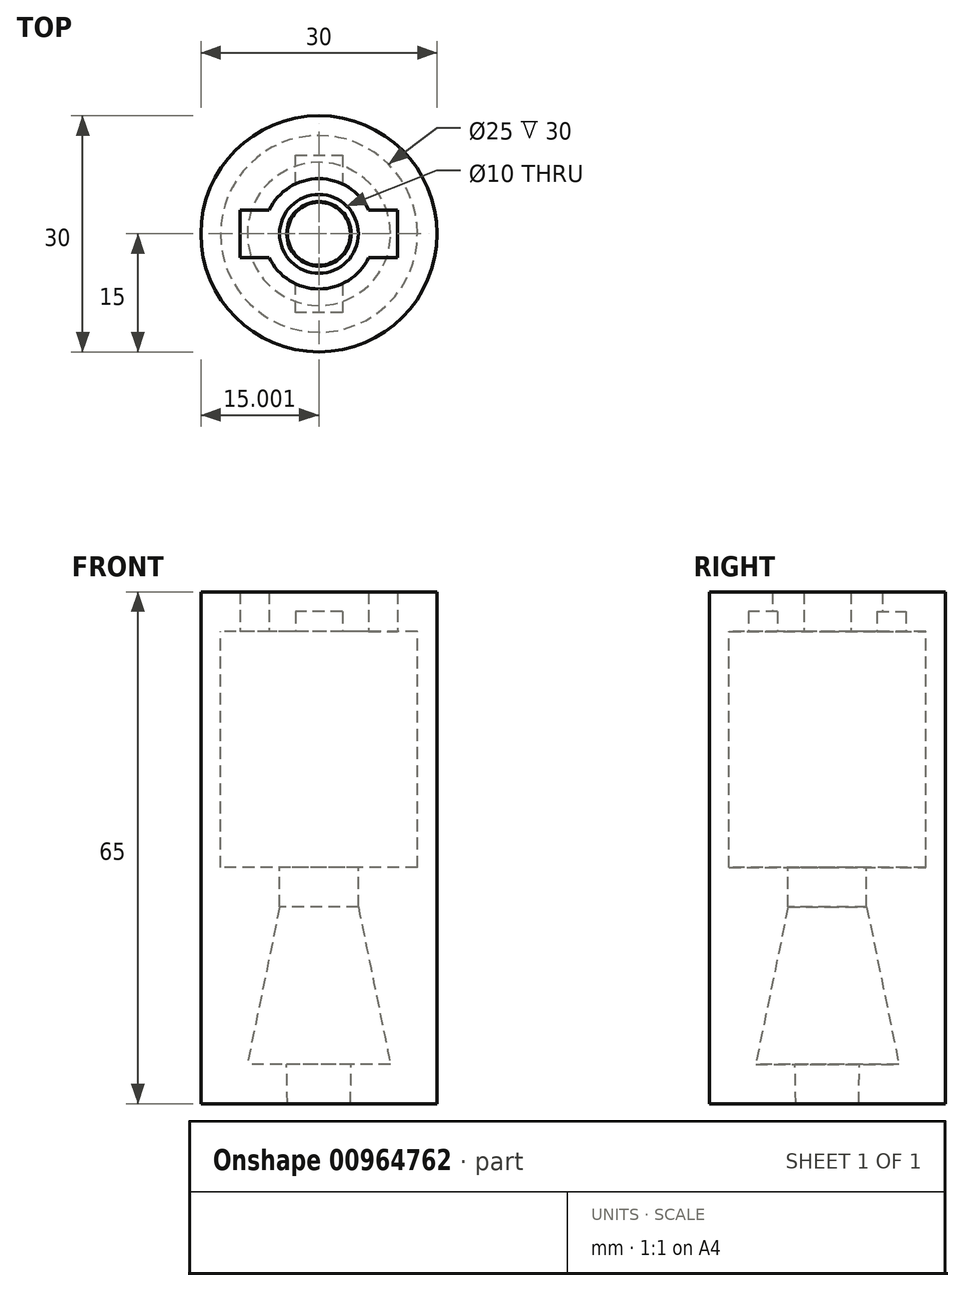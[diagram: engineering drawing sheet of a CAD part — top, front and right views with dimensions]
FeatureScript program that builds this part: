
annotation { "Feature Type Name" : "Feature", "Feature Type Description" : "" }
export const myFeature = defineFeature(function(context is Context, id is Id, definition is map)
    precondition{}
    {
        {
            var Q0;
            Q0=qCreatedBy(makeId("Front.planeOp"),FACE);
            var sketch = newSketch(context, id + "F0", { "sketchPlane" : qUnion([Q0])});
            skArc(sketch, "E0", {"start": v(-36.6, 33.12) * mm, "mid": v(-51.6, 48.12) * mm, "end": v(-66.6, 33.12) * mm});
            skArc(sketch, "E1", {"start": v(-45.27, 36.12) * mm, "mid": v(-46.65, 38.07) * mm, "end": v(-48.6, 39.45) * mm});
            skLineSegment(sketch, "E2.bottom", {"start": v(-54.6, 43.12) * mm, "end": v(-48.6, 43.12) * mm});
            skPoint(sketch, "E3", {"position": v(-51.6, 43.12) * mm});
            skArc(sketch, "E4.trimOffspring", {"start": v(-54.6, 39.45) * mm, "mid": v(-56.55, 38.07) * mm, "end": v(-57.92, 36.12) * mm});
            skCircle(sketch, "E5", {"center": v(-51.6, 33.12) * mm, "radius": 15 * mm});
            skArc(sketch, "E6", {"start": v(-48.6, 26.8) * mm, "mid": v(-46.65, 28.17) * mm, "end": v(-45.27, 30.12) * mm});
            skLineSegment(sketch, "E7", {"start": v(-48.6, 43.12) * mm, "end": v(-48.6, 39.45) * mm});
            skLineSegment(sketch, "E8", {"start": v(-48.6, 23.12) * mm, "end": v(-54.6, 23.12) * mm});
            skLineSegment(sketch, "E9", {"start": v(-54.6, 23.12) * mm, "end": v(-54.6, 26.8) * mm});
            skLineSegment(sketch, "E10.trimOffspring", {"start": v(-54.6, 39.45) * mm, "end": v(-54.6, 43.12) * mm});
            skLineSegment(sketch, "E11.trimOffspring", {"start": v(-48.6, 26.8) * mm, "end": v(-48.6, 23.12) * mm});
            skArc(sketch, "E12.1.0", {"start": v(-57.92, 30.12) * mm, "mid": v(-56.55, 28.17) * mm, "end": v(-54.6, 26.8) * mm});
            skLineSegment(sketch, "E12.1.1", {"start": v(-61.6, 36.12) * mm, "end": v(-57.92, 36.12) * mm});
            skLineSegment(sketch, "E12.1.2", {"start": v(-41.6, 36.12) * mm, "end": v(-41.6, 30.12) * mm});
            skLineSegment(sketch, "E12.1.4", {"start": v(-61.6, 30.12) * mm, "end": v(-61.6, 36.12) * mm});
            skLineSegment(sketch, "E12.1.5", {"start": v(-41.6, 30.12) * mm, "end": v(-45.27, 30.12) * mm});
            skPoint(sketch, "E12.1.6", {"position": v(-41.6, 33.12) * mm});
            skLineSegment(sketch, "E12.1.7", {"start": v(-45.27, 36.12) * mm, "end": v(-41.6, 36.12) * mm});
            skLineSegment(sketch, "E12.1.9", {"start": v(-57.92, 30.12) * mm, "end": v(-61.6, 30.12) * mm});
            skPoint(sketch, "E12.2.6", {"position": v(-51.6, 23.12) * mm});
            skArc(sketch, "E12.2.8", {"start": v(-57.92, 30.12) * mm, "mid": v(-56.55, 28.17) * mm, "end": v(-54.6, 26.8) * mm});
            skLineSegment(sketch, "E12.anchor1", {"start": v(-51.6, 33.12) * mm, "end": v(-54.6, 23.12) * mm, "construction": true});
            skLineSegment(sketch, "E12.anchor2", {"start": v(-51.6, 33.12) * mm, "end": v(-48.6, 43.12) * mm, "construction": true});
            skPoint(sketch, "E13.orphan", {"position": v(-51.6, 40.12) * mm});
            skPoint(sketch, "E14.orphan", {"position": v(-44.6, 33.12) * mm});
            skPoint(sketch, "E15.orphan", {"position": v(-51.6, 26.12) * mm});
            skPoint(sketch, "E16.orphan", {"position": v(-58.6, 33.12) * mm});
            skSolve(sketch);
        }
        {
            var Q0;
            Q0=makeQuery(id+"F0.imprint","IMPRINT",FACE,{"disambiguationData":[TD([[makeQuery(id+"F0.imprint","IMPRINT",EDGE,{"derivedFrom":sQuery(id+"F0.wireOp",EDGE,"E5")}),1.0]])]});
            extrude(context, id + "F1", {"entities" : qUnion([Q0]), "depth" : 2.5 * mm, "offsetDistance" : 25 * mm});
        }
        {
            var Q0;
            Q0=makeQuery(id+"F1.opExtrude","CAP_FACE",FACE,{"disambiguationData":[OSD([sQuery(id+"F0.wireOp",EDGE,"E2.bottom"),sQuery(id+"F0.wireOp",EDGE,"E5"),sQuery(id+"F0.wireOp",EDGE,"E6"),sQuery(id+"F0.wireOp",EDGE,"E7"),sQuery(id+"F0.wireOp",EDGE,"E8"),sQuery(id+"F0.wireOp",EDGE,"E9"),sQuery(id+"F0.wireOp",EDGE,"E10.trimOffspring"),sQuery(id+"F0.wireOp",EDGE,"E11.trimOffspring"),sQuery(id+"F0.wireOp",EDGE,"E4.trimOffspring")])],"isStart":true});
            var sketch = newSketch(context, id + "F2", { "sketchPlane" : qUnion([Q0])});
            skArc(sketch, "E17", {"start": v(64.43, 40.9) * mm, "mid": v(36.77, 30.85) * mm, "end": v(66.16, 29.54) * mm});
            skArc(sketch, "E18", {"start": v(57.92, 36.12) * mm, "mid": v(51.6, 40.12) * mm, "end": v(45.27, 36.12) * mm});
            skLineSegment(sketch, "E19.bottom", {"start": v(41.6, 30.12) * mm, "end": v(41.6, 36.12) * mm});
            skPoint(sketch, "E20", {"position": v(41.6, 33.12) * mm});
            skArc(sketch, "E21.trimOffspring", {"start": v(45.27, 30.12) * mm, "mid": v(51.6, 26.12) * mm, "end": v(57.92, 30.12) * mm});
            skCircle(sketch, "E22", {"center": v(51.6, 33.12) * mm, "radius": 15 * mm});
            skLineSegment(sketch, "E23", {"start": v(41.6, 36.12) * mm, "end": v(45.27, 36.12) * mm});
            skLineSegment(sketch, "E24", {"start": v(61.6, 36.12) * mm, "end": v(61.6, 30.12) * mm});
            skLineSegment(sketch, "E25", {"start": v(61.6, 30.12) * mm, "end": v(57.92, 30.12) * mm});
            skLineSegment(sketch, "E26.trimOffspring", {"start": v(45.27, 30.12) * mm, "end": v(41.6, 30.12) * mm});
            skLineSegment(sketch, "E27.trimOffspring", {"start": v(57.92, 36.12) * mm, "end": v(61.6, 36.12) * mm});
            skArc(sketch, "E28.0", {"start": v(54.6, 39.45) * mm, "mid": v(56.55, 38.07) * mm, "end": v(57.92, 36.12) * mm});
            skArc(sketch, "E28.2", {"start": v(48.6, 26.8) * mm, "mid": v(46.65, 28.17) * mm, "end": v(45.27, 30.12) * mm});
            skArc(sketch, "E29.trimOffspring", {"start": v(45.27, 36.12) * mm, "mid": v(46.65, 38.07) * mm, "end": v(48.6, 39.45) * mm});
            skArc(sketch, "E30.trimOffspring", {"start": v(57.92, 30.12) * mm, "mid": v(56.55, 28.17) * mm, "end": v(54.6, 26.8) * mm});
            skSolve(sketch);
        }
        {
            var Q0;
            Q0 = qSketchRegion(id + "F2", true);
            extrude(context, id + "F3", {"entities" : qUnion([Q0]), "operationType" : NewBodyOperationType.ADD, "depth" : 2.5 * mm, "offsetDistance" : 25 * mm});
        }
        {
            var Q0;
            Q0=qCreatedBy(makeId("Front.planeOp"),FACE);
            var sketch = newSketch(context, id + "F4", { "sketchPlane" : qUnion([Q0])});
            skLineSegment(sketch, "E31", {"start": v(6.78, 37.47) * mm, "end": v(6.78, -22.53) * mm});
            skLineSegment(sketch, "E32", {"start": v(4.28, 37.47) * mm, "end": v(4.28, 7.47) * mm});
            skLineSegment(sketch, "E33", {"start": v(-8.22, 51.53) * mm, "end": v(-8.22, -75.92) * mm, "construction": true});
            skLineSegment(sketch, "E34", {"start": v(4.28, 7.47) * mm, "end": v(-3.22, 7.47) * mm});
            skLineSegment(sketch, "E35", {"start": v(4.28, 37.47) * mm, "end": v(6.78, 37.47) * mm});
            skLineSegment(sketch, "E36", {"start": v(6.78, -22.53) * mm, "end": v(-4.22, -22.53) * mm});
            skLineSegment(sketch, "E37", {"start": v(-4.22, -22.53) * mm, "end": v(-4.13, -17.53) * mm});
            skLineSegment(sketch, "E38", {"start": v(-4.13, -17.53) * mm, "end": v(0.87, -17.53) * mm});
            skLineSegment(sketch, "E39", {"start": v(-3.22, 7.47) * mm, "end": v(-3.22, 2.47) * mm});
            skLineSegment(sketch, "E40", {"start": v(-3.22, 2.47) * mm, "end": v(0.87, -17.53) * mm});
            skSolve(sketch);
        }
        {
            var Q0;
            Q0=makeQuery(id+"F4.imprint","IMPRINT",FACE,{"disambiguationData":[TD([[makeQuery(id+"F4.imprint","IMPRINT",EDGE,{"derivedFrom":sQuery(id+"F4.wireOp",EDGE,"E31")}),-1.0]])]});
            var Q1;
            Q1=sQuery(id+"F4.wireOp",EDGE,"E33");
            revolve(context, id + "F5", {"surfaceOperationType" : NewSurfaceOperationType.NEW, "entities" : qUnion([Q0]), "axis" : qUnion([Q1]), "revolveType" : RevolveType.FULL});
        }
        {
            var Q0;
            Q0=makeQuery(id+"F1.opExtrude","SWEPT_BODY",BODY,{"disambiguationData":[OSD([sQuery(id+"F0.wireOp",EDGE,"E5"),sQuery(id+"F0.wireOp",EDGE,"E12.1.1"),sQuery(id+"F0.wireOp",EDGE,"E12.1.2"),sQuery(id+"F0.wireOp",EDGE,"E12.1.4"),sQuery(id+"F0.wireOp",EDGE,"E12.1.5"),sQuery(id+"F0.wireOp",EDGE,"E12.1.7"),sQuery(id+"F0.wireOp",EDGE,"E12.1.9"),sQuery(id+"F0.wireOp",EDGE,"E7"),sQuery(id+"F0.wireOp",EDGE,"E8"),sQuery(id+"F0.wireOp",EDGE,"E2.bottom"),sQuery(id+"F0.wireOp",EDGE,"E9"),sQuery(id+"F0.wireOp",EDGE,"E11.trimOffspring"),sQuery(id+"F0.wireOp",EDGE,"E10.trimOffspring"),sQuery(id+"F0.wireOp",EDGE,"E4.trimOffspring"),sQuery(id+"F0.wireOp",EDGE,"E1"),sQuery(id+"F0.wireOp",EDGE,"E6"),sQuery(id+"F0.wireOp",EDGE,"E12.1.0")])]});
            var Q1;
            Q1=makeQuery(id+"F3.opExtrude","CAP_EDGE",EDGE,{"disambiguationData":[OSD([sQuery(id+"F2.wireOp",EDGE,"E23")])],"isStart":false});
            var Q2;
            Q2=makeQuery(id+"F3.opExtrude","CAP_EDGE",EDGE,{"disambiguationData":[OSD([sQuery(id+"F2.wireOp",EDGE,"E23")])],"isStart":false});
            transform(context, id + "F6", {"entities" : qUnion([Q0]), "transformType" : TransformType.ROTATION, "transformAxis" : qUnion([Q2]), "angle" : 90 * degree, "makeCopy" : false});
        }
        {
            var Q0;
            Q0=makeQuery(id+"F5.opRevolve","SWEPT_FACE",FACE,{"disambiguationData":[OSD([sQuery(id+"F4.wireOp",EDGE,"E35")])]});
            cPlane(context, id + "F7", {"entities" : qUnion([Q0]), "cplaneType" : CPlaneType.OFFSET, "offset" : 0 * mm, "width" : 150 * mm, "height" : 150 * mm});
        }
        {
            var Q0;
            Q0=qCreatedBy(id+"F7.planeOp",FACE);
            var sketch = newSketch(context, id + "F8", { "sketchPlane" : qUnion([Q0])});
            skArc(sketch, "E41", {"start": v(6.78, 0) * mm, "mid": v(-8.22, 15) * mm, "end": v(-23.22, 0) * mm});
            skArc(sketch, "E42", {"start": v(-1.9, 3) * mm, "mid": v(-3.27, 4.95) * mm, "end": v(-5.22, 6.32) * mm});
            skLineSegment(sketch, "E43.bottom", {"start": v(-11.22, 10) * mm, "end": v(-5.22, 10) * mm});
            skPoint(sketch, "E44", {"position": v(-8.22, 10) * mm});
            skArc(sketch, "E45.trimOffspring", {"start": v(-11.22, 6.32) * mm, "mid": v(-13.17, 4.95) * mm, "end": v(-14.54, 3) * mm});
            skCircle(sketch, "E46", {"center": v(-8.22, 0) * mm, "radius": 15 * mm});
            skArc(sketch, "E47", {"start": v(-5.22, -6.32) * mm, "mid": v(-3.27, -4.95) * mm, "end": v(-1.9, -3) * mm});
            skLineSegment(sketch, "E48", {"start": v(-5.22, 10) * mm, "end": v(-5.22, 6.32) * mm});
            skLineSegment(sketch, "E49", {"start": v(-5.22, -10) * mm, "end": v(-11.22, -10) * mm});
            skLineSegment(sketch, "E50", {"start": v(-11.22, -10) * mm, "end": v(-11.22, -6.32) * mm});
            skLineSegment(sketch, "E51.trimOffspring", {"start": v(-11.22, 6.32) * mm, "end": v(-11.22, 10) * mm});
            skLineSegment(sketch, "E52.trimOffspring", {"start": v(-5.22, -6.32) * mm, "end": v(-5.22, -10) * mm});
            skArc(sketch, "E53.1.0", {"start": v(-14.54, -3) * mm, "mid": v(-13.17, -4.95) * mm, "end": v(-11.22, -6.32) * mm});
            skLineSegment(sketch, "E53.1.1", {"start": v(-18.22, 3) * mm, "end": v(-14.54, 3) * mm});
            skLineSegment(sketch, "E53.1.2", {"start": v(1.78, 3) * mm, "end": v(1.78, -3) * mm});
            skLineSegment(sketch, "E53.1.4", {"start": v(-18.22, -3) * mm, "end": v(-18.22, 3) * mm});
            skLineSegment(sketch, "E53.1.5", {"start": v(1.78, -3) * mm, "end": v(-1.9, -3) * mm});
            skPoint(sketch, "E53.1.6", {"position": v(1.78, 0) * mm});
            skLineSegment(sketch, "E53.1.7", {"start": v(-1.9, 3) * mm, "end": v(1.78, 3) * mm});
            skLineSegment(sketch, "E53.1.9", {"start": v(-14.54, -3) * mm, "end": v(-18.22, -3) * mm});
            skPoint(sketch, "E53.2.6", {"position": v(-8.22, -10) * mm});
            skArc(sketch, "E53.2.8", {"start": v(-14.54, -3) * mm, "mid": v(-13.17, -4.95) * mm, "end": v(-11.22, -6.32) * mm});
            skLineSegment(sketch, "E53.anchor1", {"start": v(-8.22, 0) * mm, "end": v(-11.22, -10) * mm, "construction": true});
            skLineSegment(sketch, "E53.anchor2", {"start": v(-8.22, 0) * mm, "end": v(-5.22, 10) * mm, "construction": true});
            skPoint(sketch, "E54.orphan", {"position": v(-8.22, 7) * mm});
            skPoint(sketch, "E55.orphan", {"position": v(-1.22, 0) * mm});
            skPoint(sketch, "E56.orphan", {"position": v(-8.22, -7) * mm});
            skPoint(sketch, "E57.orphan", {"position": v(-15.22, 0) * mm});
            skCircle(sketch, "E58.0.0", {"center": v(-8.22, 0) * mm, "radius": 12.5 * mm});
            skSolve(sketch);
        }
        {
            var Q0;
            Q0=makeQuery(id+"F8.imprint","IMPRINT",FACE,{"disambiguationData":[TD([[makeQuery(id+"F8.imprint","IMPRINT",EDGE,{"derivedFrom":sQuery(id+"F8.wireOp",EDGE,"E46")}),1.0]])]});
            extrude(context, id + "F9", {"entities" : qUnion([Q0]), "operationType" : NewBodyOperationType.ADD, "depth" : 2.5 * mm, "offsetDistance" : 25 * mm});
        }
        {
            var Q0;
            Q0=makeQuery(id+"F8.imprint","IMPRINT",FACE,{"disambiguationData":[TD([[makeQuery(id+"F8.imprint","IMPRINT",EDGE,{"derivedFrom":sQuery(id+"F8.wireOp",EDGE,"E53.1.1")}),1.0]])]});
            extrude(context, id + "F10", {"entities" : qUnion([Q0]), "operationType" : NewBodyOperationType.ADD, "depth" : 2.5 * mm, "offsetDistance" : 25 * mm});
        }
        {
            var Q0;
            {var subQ0=sQuery(id+"F8.wireOp",EDGE,"E58.0.0");Q0=makeQuery(id+"F10.boolean.opBoolean","MERGE",FACE,{"derivedFrom":[makeQuery(id+"F9.opExtrude","CAP_FACE",FACE,{"disambiguationData":[OSD([sQuery(id+"F8.wireOp",EDGE,"E46"),subQ0])],"isStart":false}),makeQuery(id+"F10.opExtrude","CAP_FACE",FACE,{"disambiguationData":[OSD([sQuery(id+"F8.wireOp",EDGE,"E53.1.1"),sQuery(id+"F8.wireOp",EDGE,"E53.1.2"),sQuery(id+"F8.wireOp",EDGE,"E53.1.4"),sQuery(id+"F8.wireOp",EDGE,"E53.1.5"),sQuery(id+"F8.wireOp",EDGE,"E53.1.7"),sQuery(id+"F8.wireOp",EDGE,"E53.1.9"),sQuery(id+"F8.wireOp",EDGE,"E48"),sQuery(id+"F8.wireOp",EDGE,"E49"),sQuery(id+"F8.wireOp",EDGE,"E43.bottom"),sQuery(id+"F8.wireOp",EDGE,"E50"),sQuery(id+"F8.wireOp",EDGE,"E52.trimOffspring"),sQuery(id+"F8.wireOp",EDGE,"E51.trimOffspring"),sQuery(id+"F8.wireOp",EDGE,"E45.trimOffspring"),sQuery(id+"F8.wireOp",EDGE,"E42"),sQuery(id+"F8.wireOp",EDGE,"E47"),sQuery(id+"F8.wireOp",EDGE,"E53.1.0"),subQ0])],"isStart":false})]});}
            cPlane(context, id + "F11", {"entities" : qUnion([Q0]), "cplaneType" : CPlaneType.OFFSET, "offset" : 2.5 * mm, "width" : 150 * mm, "height" : 150 * mm});
        }
        {
            var Q0;
            Q0=qCreatedBy(id+"F11.planeOp",FACE);
            var sketch = newSketch(context, id + "F12", { "sketchPlane" : qUnion([Q0])});
            skArc(sketch, "E59", {"start": v(4.6, 7.78) * mm, "mid": v(-23.05, -2.27) * mm, "end": v(6.35, -3.58) * mm});
            skArc(sketch, "E60", {"start": v(-1.9, 3) * mm, "mid": v(-8.22, 7) * mm, "end": v(-14.54, 3) * mm});
            skLineSegment(sketch, "E61.bottom", {"start": v(-18.22, -3) * mm, "end": v(-18.22, 3) * mm});
            skPoint(sketch, "E62", {"position": v(-18.22, 0) * mm});
            skArc(sketch, "E63.trimOffspring", {"start": v(-14.54, -3) * mm, "mid": v(-8.22, -7) * mm, "end": v(-1.9, -3) * mm});
            skCircle(sketch, "E64", {"center": v(-8.22, 0) * mm, "radius": 15 * mm});
            skLineSegment(sketch, "E65", {"start": v(-18.22, 3) * mm, "end": v(-14.54, 3) * mm});
            skLineSegment(sketch, "E66", {"start": v(1.78, 3) * mm, "end": v(1.78, -3) * mm});
            skLineSegment(sketch, "E67", {"start": v(1.78, -3) * mm, "end": v(-1.9, -3) * mm});
            skLineSegment(sketch, "E68.trimOffspring", {"start": v(-14.54, -3) * mm, "end": v(-18.22, -3) * mm});
            skLineSegment(sketch, "E69.trimOffspring", {"start": v(-1.9, 3) * mm, "end": v(1.78, 3) * mm});
            skArc(sketch, "E70.0", {"start": v(-5.22, 6.32) * mm, "mid": v(-3.27, 4.95) * mm, "end": v(-1.9, 3) * mm});
            skArc(sketch, "E70.2", {"start": v(-11.22, -6.32) * mm, "mid": v(-13.17, -4.95) * mm, "end": v(-14.54, -3) * mm});
            skArc(sketch, "E71.trimOffspring", {"start": v(-14.54, 3) * mm, "mid": v(-13.17, 4.95) * mm, "end": v(-11.22, 6.32) * mm});
            skArc(sketch, "E72.trimOffspring", {"start": v(-1.9, -3) * mm, "mid": v(-3.27, -4.95) * mm, "end": v(-5.22, -6.32) * mm});
            skSolve(sketch);
        }
        {
            var Q0;
            Q0=makeQuery(id+"F12.imprint","IMPRINT",FACE,{"disambiguationData":[TD([[makeQuery(id+"F12.imprint","IMPRINT",EDGE,{"derivedFrom":sQuery(id+"F12.wireOp",EDGE,"E61.bottom")}),1.0]])]});
            extrude(context, id + "F13", {"entities" : qUnion([Q0]), "operationType" : NewBodyOperationType.ADD, "oppositeDirection" : true, "depth" : 2.5 * mm, "offsetDistance" : 25 * mm});
        }
        {
            var Q0;
            Q0=makeQuery(id+"F1.opExtrude","SWEPT_BODY",BODY,{"disambiguationData":[OSD([sQuery(id+"F0.wireOp",EDGE,"E5"),sQuery(id+"F0.wireOp",EDGE,"E12.1.1"),sQuery(id+"F0.wireOp",EDGE,"E12.1.2"),sQuery(id+"F0.wireOp",EDGE,"E12.1.4"),sQuery(id+"F0.wireOp",EDGE,"E12.1.5"),sQuery(id+"F0.wireOp",EDGE,"E12.1.7"),sQuery(id+"F0.wireOp",EDGE,"E12.1.9"),sQuery(id+"F0.wireOp",EDGE,"E7"),sQuery(id+"F0.wireOp",EDGE,"E8"),sQuery(id+"F0.wireOp",EDGE,"E2.bottom"),sQuery(id+"F0.wireOp",EDGE,"E9"),sQuery(id+"F0.wireOp",EDGE,"E11.trimOffspring"),sQuery(id+"F0.wireOp",EDGE,"E10.trimOffspring"),sQuery(id+"F0.wireOp",EDGE,"E4.trimOffspring"),sQuery(id+"F0.wireOp",EDGE,"E1"),sQuery(id+"F0.wireOp",EDGE,"E6"),sQuery(id+"F0.wireOp",EDGE,"E12.1.0")])]});
            deleteBodies(context, id + "F14", {"entities" : qUnion([Q0])});
        }
    });
